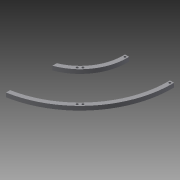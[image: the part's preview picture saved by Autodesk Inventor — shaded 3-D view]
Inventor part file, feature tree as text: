
AUTODESK INVENTOR PART (.ipt)
format: ipt  version: 2013 (Build 170138000, 138)  size: 119,808 bytes
history: native  units: in
note: dims shown in document units (in); Inventor stores cm internally (conversion verified against a paired STEP export)
features: extrude x2, sketch x2, projected_geometry x1
ambient origin geometry x8: Origin, YZ Plane, XZ Plane, XY Plane, X Axis, Y Axis, Z Axis, Center Point
bodies: Solid1 (feature_tree)
feature tree (5):
  extrude  "Extrusion1"  Depth=0.5in TaperAngle=0.0deg
  extrude  "Extrusion2"  Depth=0.266in
  sketch  "Sketch1"  dims[d0=2.0in d1=0.5in d2=0.0in]
  sketch  "Sketch2"  dims[d3=0.266in d4=0.266in d5=0.266in d6=0.266in d7=0.266in d8=0.266in d9=0.5in d10=0.0in]
  projected_geometry  "Projected Loop1"
